# Revit family: H_e130
name_source: partatom
category: Generic Models
revit_build: Autodesk Revit 2018 (Build: 20170223_1515(x64)
units: mm (PartAtom-declared; Revit-internal decimal feet)

## family parameters
Always vertical = No
Can host rebar = No
Cut with Voids When Loaded = No
Part Type = Normal
Room Calculation Point = No
Round Connector Dimension = Use Diameter
Shared = No
Work Plane-Based = No

## types (2) — shared parameters
A = 1 A
Clearence = 26 "
DI_IN_Int = 2 "
DI_IN_out = 3 "
DI_Out_out = 3 "
DI_out_int = 3 "
D_EA_H = 3 "
D_EA_L = 3 "
D_OA_H = 4 "
D_OA_L = 4 "
D_RA_H = 4 "
D_RA_L = 4 "
D_SA_H = 5 "
D_SA_L = 3 "
Drain_Con_H = 1 "
Drain_Con_L = 10 "
E_Con_L = 1 "
E_con_H = 9 "
Fan Number = 2
Filter number = 2
Hauteur = 9 "
Largeur = 23 "
Longueur = 24 "
MaxDucking = 2 "
Weight = 35.00 lb
Weight on expedition = 41.00 lb

## per-type parameters (varying)
| type | Drain |
| E130 | No |
| H130 | Yes |

## geometry (parser evidence)
native form markers: Sweep x2
no freeform markers — native parametric forms only
